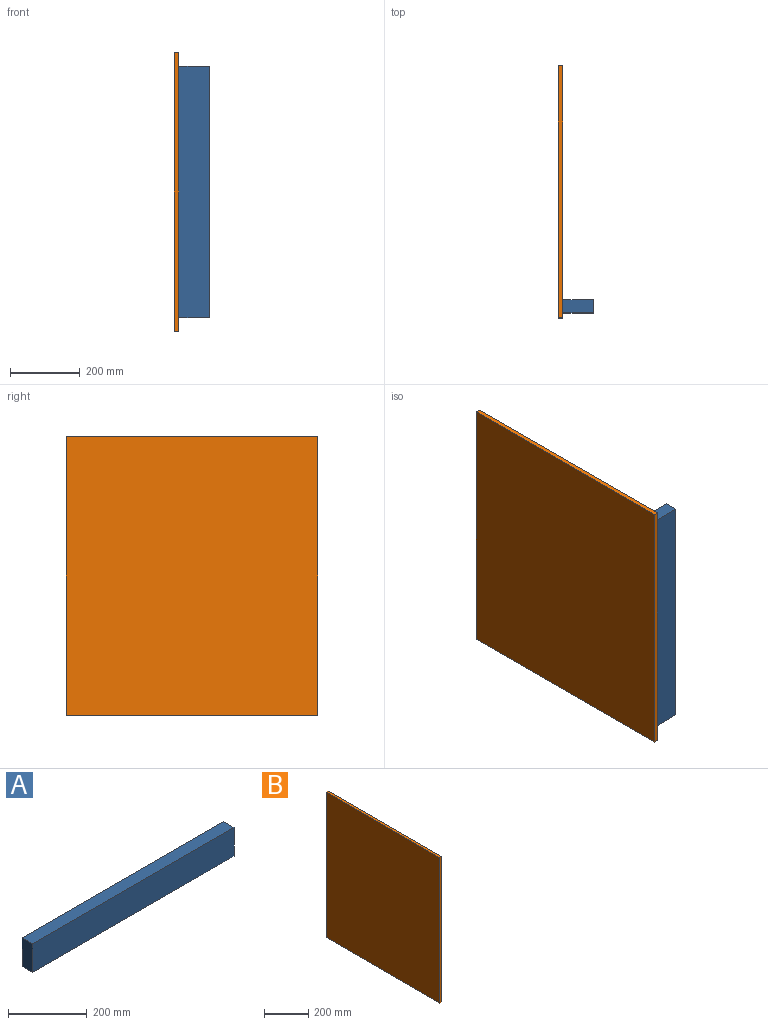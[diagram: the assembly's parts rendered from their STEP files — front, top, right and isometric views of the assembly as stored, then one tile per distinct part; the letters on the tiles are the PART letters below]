
ASSEMBLY  parts=2 mates=1
PART A: 6 faces, bbox 723.9x38.1x88.9 mm
  f0: plane 723.9x38.1mm, normal (0,0,1), area 27580.6mm2, adj f1,f3,f4,f5
  f1: plane 88.9x38.1mm, normal (-1,0,0), area 3387.1mm2, adj f0,f2,f4,f5
  f2: plane 723.9x38.1mm, normal (0,0,-1), area 27580.6mm2, adj f1,f3,f4,f5
  f3: plane 88.9x38.1mm, normal (1,0,0), area 3387.1mm2, adj f0,f2,f4,f5
  f4: plane 723.9x88.9mm, normal (0,-1,0), area 64354.7mm2, adj f0,f1,f2,f3
  f5: plane 723.9x88.9mm, normal (0,1,0), area 64354.7mm2, adj f0,f1,f2,f3
PART B: 6 faces, bbox 12.7x723.9x800.1 mm
  f0: plane 723.9x12.7mm, normal (0,0,1), area 9193.5mm2, adj f1,f3,f4,f5
  f1: plane 800.1x12.7mm, normal (0,-1,0), area 10161.3mm2, adj f0,f2,f4,f5
  f2: plane 723.9x12.7mm, normal (0,0,-1), area 9193.5mm2, adj f1,f3,f4,f5
  f3: plane 800.1x12.7mm, normal (0,1,0), area 10161.3mm2, adj f0,f2,f4,f5
  f4: plane 800.1x723.9mm, normal (1,0,0), area 579192.4mm2, adj f0,f1,f2,f3
  f5: plane 800.1x723.9mm, normal (-1,0,0), area 579192.4mm2, adj f0,f1,f2,f3
PLACE A rot(axis=(0,1,0),90deg) t=(293.97,-33.98,367.63)mm
PLACE B t=(269.03,273.14,176.71)mm fixed
MATE planar A.f2 <-> B.f4  axis (-1,0,0) through (281.73,-53.03,186.42)mm
